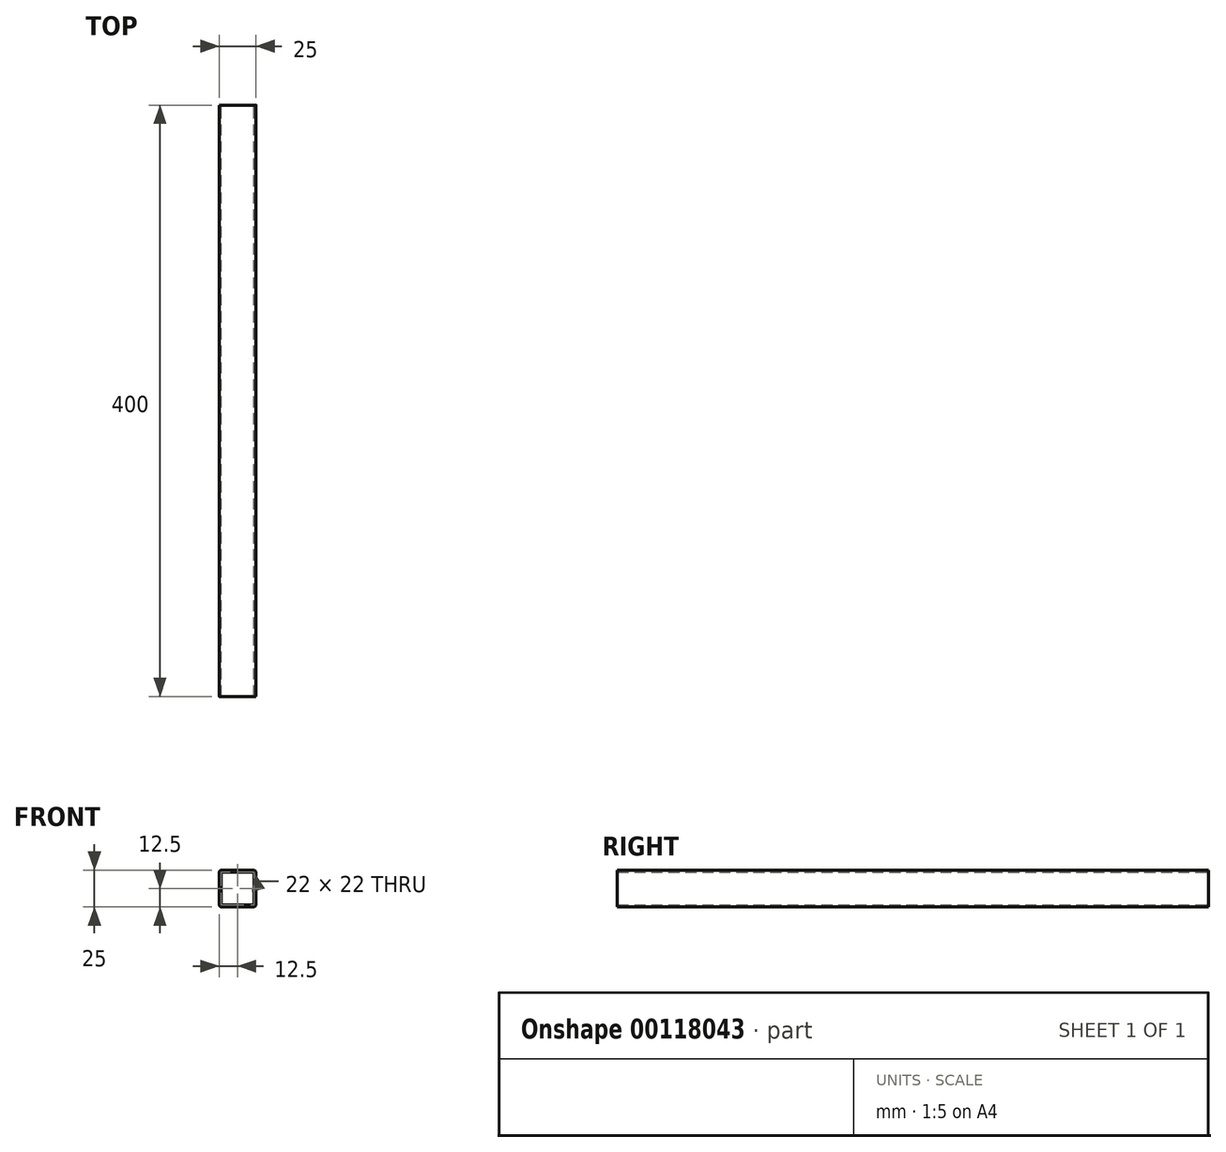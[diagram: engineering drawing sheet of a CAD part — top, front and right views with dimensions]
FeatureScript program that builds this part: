
annotation { "Feature Type Name" : "Feature", "Feature Type Description" : "" }
export const myFeature = defineFeature(function(context is Context, id is Id, definition is map)
    precondition{}
    {
        {
            var Q0;
            Q0=qCreatedBy(makeId("Front.planeOp"),FACE);
            var sketch = newSketch(context, id + "F0", { "sketchPlane" : qUnion([Q0])});
            skLineSegment(sketch, "E0.bottom", {"start": v(2, 0) * mm, "end": v(23, 0) * mm});
            skLineSegment(sketch, "E0.top", {"start": v(2, 25) * mm, "end": v(23, 25) * mm});
            skLineSegment(sketch, "E0.left", {"start": v(0, 2) * mm, "end": v(0, 23) * mm});
            skLineSegment(sketch, "E0.right", {"start": v(25, 2) * mm, "end": v(25, 23) * mm});
            skPoint(sketch, "E1.visualSharp", {"position": v(0, 25) * mm});
            skArc(sketch, "E1.filletArc", {"start": v(2, 25) * mm, "mid": v(0.59, 24.41) * mm, "end": v(0, 23) * mm});
            skPoint(sketch, "E2.visualSharp", {"position": v(25, 25) * mm});
            skArc(sketch, "E2.filletArc", {"start": v(25, 23) * mm, "mid": v(24.41, 24.41) * mm, "end": v(23, 25) * mm});
            skPoint(sketch, "E3.visualSharp", {"position": v(25, 0) * mm});
            skArc(sketch, "E3.filletArc", {"start": v(23, 0) * mm, "mid": v(24.41, 0.59) * mm, "end": v(25, 2) * mm});
            skPoint(sketch, "E4.visualSharp", {"position": v(0, 0) * mm});
            skArc(sketch, "E4.filletArc", {"start": v(0, 2) * mm, "mid": v(0.59, 0.59) * mm, "end": v(2, 0) * mm});
            skLineSegment(sketch, "E5.0", {"start": v(1.5, 23.5) * mm, "end": v(23.5, 23.5) * mm});
            skLineSegment(sketch, "E5.1", {"start": v(1.5, 1.5) * mm, "end": v(1.5, 23.5) * mm});
            skLineSegment(sketch, "E5.2", {"start": v(1.5, 1.5) * mm, "end": v(23.5, 1.5) * mm});
            skLineSegment(sketch, "E5.3", {"start": v(23.5, 1.5) * mm, "end": v(23.5, 23.5) * mm});
            skSolve(sketch);
        }
        {
            var Q0;
            Q0=makeQuery(id+"F0.imprint","IMPRINT",FACE,{"disambiguationData":[TD([[makeQuery(id+"F0.imprint","IMPRINT",EDGE,{"derivedFrom":sQuery(id+"F0.wireOp",EDGE,"E0.bottom")}),1.0]])]});
            extrude(context, id + "F1", {"entities" : qUnion([Q0]), "depth" : 400 * mm});
        }
    });
